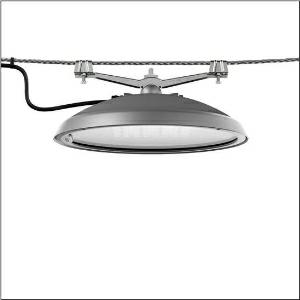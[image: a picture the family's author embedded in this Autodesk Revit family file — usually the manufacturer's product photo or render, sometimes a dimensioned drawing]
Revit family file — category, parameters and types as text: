
# Revit family: dl_r__50_iq_mini___p1_0s_5xa248u31f08ge_4109
name_source: partatom
category: Lighting Fixtures
units: mm (PartAtom-declared; Revit-internal decimal feet)

## family parameters
Cut with Voids When Loaded = No
Host = Face
Light Source = No
Part Type = Normal
Room Calculation Point = No
Round Connector Dimension = Use Diameter
Shared = No

## types (1)
- --- (1 x LED, 5030 lm, 32.7 W, 3000K)
    Apparent Load = 33 VA
    CIE Flux Codes = 23 54 93 100 100
    Color Rendering = 70
    Color Temperature = 3000K
    Default Elevation = 1800 mm
    Description = DL® 50 iQ mini, catenary luminaire, primary light control with lens, of PMMA, primary optical cover: cover, of toughened safety glass, transparent, light distribution: P1.0s, light emission: direct distribution, primary light characteristic: symmetric, installation type: suspended mounting, LED, High Power LED, rated luminous flux: 5.030lm, luminous efficacy: 154lm/W, light colour: 730, colour temperature: 3000K, control gear: iQ Street-Remote, control: optimised constant luminous flux control (CLO 2.0), Desk-Remote (wireless, voltage-free reading and setting of iQ features in the workshop via application-optimized NFC function/RFID function), Light-Fading, Smart-Wire, Night-Set, Lumen-Switch, Temp-Guard, Auto-Match, Street-Remote, mains connection: 230..240V, AC, 50/60Hz, start of lifetime: 33W, end of service life: 34W, reduction: 16W, luminaire housing, of diecast aluminium, powder-coated, Siteco® metallic grey (DB 702S), diameter: 500mm, height: 115mm, mounting height: 4..12m, protection rating (complete): IP66, insulation class (complete): insulation class II (safety insulation), certification: CE, ENEC, ENEC+, VDE, impact resistance: IK08, permissible operating ambient temperature for outdoor applications: -25..+40°C, standard-compliant lighting for roads and squares, packaging unit: 1 piece

Light Distribution: P1.0s
    Height = 124 mm  [stored 0.406824 ft]
    Lamp = 1 x LED
    Lamp Light Flux = 5030 lm
    Lamp Power = 32.7 W
    Lamp count = 1
    Length = 500 mm
    Luminous efficacy = 154 lm/W
    Manufacturer = Siteco
    ModVariant = No
    Model = 5XA248U31F08GE
    Number of Poles = 1
    OnlyDefault = Yes
    Power Factor = 1
    Product Name = DL® 50 iQ mini | P1.0s
    Product group = catenary luminaire
    ProductGroupID = 6300
    Protection Class = Protection class II
    Protection Degree = IP 66
    RLX_Detail_Level = 1
    RLX_Emergency_Light_Flux = 0 lm
    RLX_Emergency_Type = 0
    RLX_Emergency_Type_DB = No
    RlxData = <blob elided: 123581 chars, md5=7e086e7a>
    Socket = socket
    Standby Power = 0 W
    System Light Flux = 5030 lm
    System Power = 33 W
    Type Comments = factory setting: luminous flux: 100 % | dim-lin: 254 | 340 mA
    Type Image = l_1242791.jpg
    URL = http://relux.com
    VarID = @adj_161701
    Voltage = 0 V
    Weight = 0.00 kg
    Width = 0 mm  [stored 0 ft]

note: [stored X ft] marks values corroborated as IEEE doubles in the binary element streams (Revit-internal decimal feet)

## geometry (parser evidence)
native form markers: Blend x4, Sweep x12
no freeform markers — native parametric forms only
